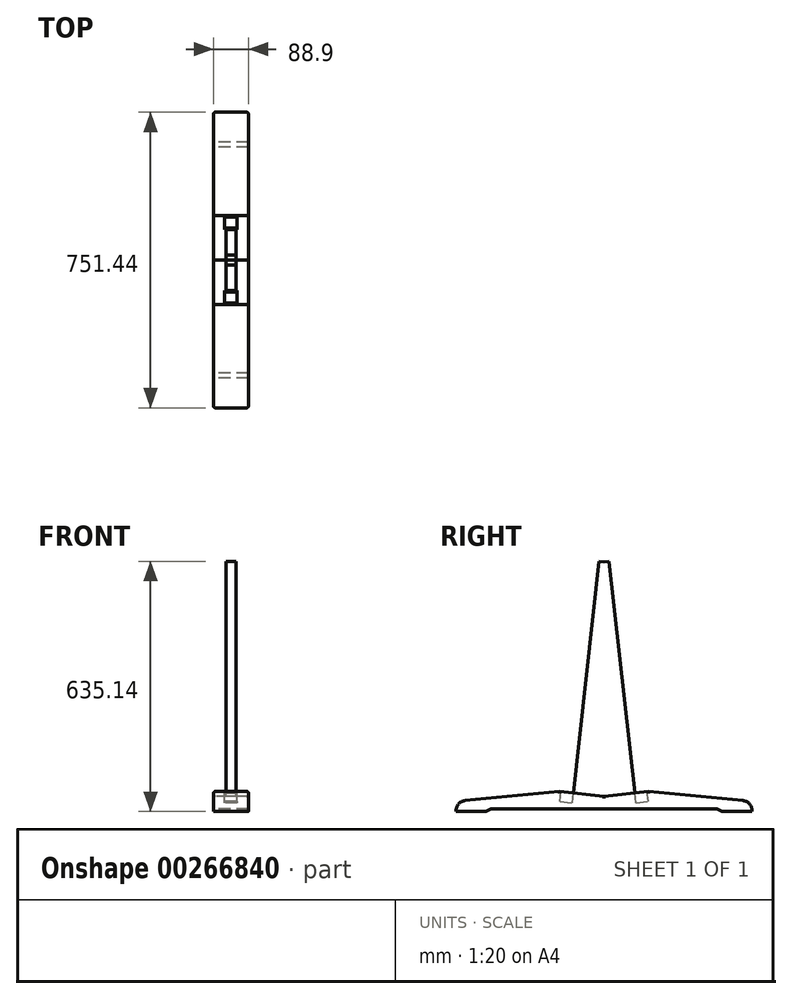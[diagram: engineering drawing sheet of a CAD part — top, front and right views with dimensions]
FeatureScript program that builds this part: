
annotation { "Feature Type Name" : "Feature", "Feature Type Description" : "" }
export const myFeature = defineFeature(function(context is Context, id is Id, definition is map)
    precondition{}
    {
        {
            var Q0;
            Q0=qCreatedBy(makeId("Right.planeOp"),FACE);
            var sketch = newSketch(context, id + "F0", { "sketchPlane" : qUnion([Q0])});
            skLineSegment(sketch, "E0", {"start": v(0, 83.9) * mm, "end": v(-112.69, 96.43) * mm});
            skLineSegment(sketch, "E1", {"start": v(-112.69, 96.43) * mm, "end": v(-352.76, 73.25) * mm});
            skLineSegment(sketch, "E2", {"start": v(-375.72, 47.96) * mm, "end": v(-375.72, 45.63) * mm});
            skLineSegment(sketch, "E3", {"start": v(-375.72, 45.63) * mm, "end": v(-299.52, 45.63) * mm});
            skLineSegment(sketch, "E4", {"start": v(-299.52, 45.63) * mm, "end": v(-286.82, 51.98) * mm});
            skLineSegment(sketch, "E5", {"start": v(-286.82, 51.98) * mm, "end": v(0, 51.98) * mm});
            skLineSegment(sketch, "E6", {"start": v(0, 83.9) * mm, "end": v(0, 51.98) * mm});
            skLineSegment(sketch, "E7.MirrorCS", {"start": v(0, 83.9) * mm, "end": v(112.69, 96.43) * mm});
            skLineSegment(sketch, "E8.MirrorCS", {"start": v(112.69, 96.43) * mm, "end": v(352.76, 73.25) * mm});
            skLineSegment(sketch, "E9.MirrorCS", {"start": v(375.72, 47.96) * mm, "end": v(375.72, 45.63) * mm});
            skLineSegment(sketch, "E10.MirrorCS", {"start": v(375.72, 45.63) * mm, "end": v(299.52, 45.63) * mm});
            skLineSegment(sketch, "E11.MirrorCS", {"start": v(286.82, 51.98) * mm, "end": v(0, 51.98) * mm});
            skLineSegment(sketch, "E12.MirrorCS", {"start": v(299.52, 45.63) * mm, "end": v(286.82, 51.98) * mm});
            skPoint(sketch, "E13.visualSharp", {"position": v(-375.72, 71.03) * mm});
            skArc(sketch, "E13.filletArc", {"start": v(-352.76, 73.25) * mm, "mid": v(-369.12, 65.04) * mm, "end": v(-375.72, 47.96) * mm});
            skPoint(sketch, "E14.visualSharp", {"position": v(375.72, 71.03) * mm});
            skArc(sketch, "E14.filletArc", {"start": v(375.72, 47.96) * mm, "mid": v(369.12, 65.04) * mm, "end": v(352.76, 73.25) * mm});
            skSolve(sketch);
        }
        {
            var Q0;
            Q0 = qSketchRegion(id + "F0", true);
            extrude(context, id + "F1", {"entities" : qUnion([Q0]), "endBound" : BoundingType.SYMMETRIC, "depth" : 88.9 * mm});
        }
        {
            var Q0;
            Q0=makeQuery(id+"F1.opExtrude","SWEPT_FACE",FACE,{"disambiguationData":[OSD([sQuery(id+"F0.wireOp",EDGE,"E0")])]});
            var sketch = newSketch(context, id + "F2", { "sketchPlane" : qUnion([Q0])});
            skLineSegment(sketch, "E15.bottom", {"start": v(15.88, -119.47) * mm, "end": v(-15.88, -119.47) * mm});
            skLineSegment(sketch, "E15.top", {"start": v(15.87, -87.72) * mm, "end": v(-15.88, -87.72) * mm});
            skLineSegment(sketch, "E15.left", {"start": v(15.88, -119.47) * mm, "end": v(15.87, -87.72) * mm});
            skLineSegment(sketch, "E15.right", {"start": v(-15.88, -119.47) * mm, "end": v(-15.88, -87.72) * mm});
            skSolve(sketch);
        }
        {
            var Q0;
            Q0=makeQuery(id+"F2.imprint","IMPRINT",FACE,{"disambiguationData":[TD([[makeQuery(id+"F2.imprint","IMPRINT",EDGE,{"derivedFrom":sQuery(id+"F2.wireOp",EDGE,"E15.bottom")}),-1.0]])]});
            extrude(context, id + "F3", {"entities" : qUnion([Q0]), "operationType" : NewBodyOperationType.REMOVE, "oppositeDirection" : true, "depth" : 25.4 * mm});
        }
        {
            var Q0;
            Q0=makeQuery(id+"F1.opExtrude","SWEPT_FACE",FACE,{"disambiguationData":[OSD([sQuery(id+"F0.wireOp",EDGE,"E7.MirrorCS")])]});
            var sketch = newSketch(context, id + "F4", { "sketchPlane" : qUnion([Q0])});
            skLineSegment(sketch, "E16.bottom", {"start": v(-15.87, 87.72) * mm, "end": v(15.88, 87.72) * mm});
            skLineSegment(sketch, "E16.top", {"start": v(-15.88, 119.47) * mm, "end": v(15.88, 119.47) * mm});
            skLineSegment(sketch, "E16.left", {"start": v(-15.88, 87.72) * mm, "end": v(-15.88, 119.47) * mm});
            skLineSegment(sketch, "E16.right", {"start": v(15.88, 87.72) * mm, "end": v(15.87, 119.47) * mm});
            skPoint(sketch, "E16.middle", {"position": v(0, 103.6) * mm});
            skSolve(sketch);
        }
        {
            var Q0;
            Q0=makeQuery(id+"F4.imprint","IMPRINT",FACE,{"disambiguationData":[TD([[makeQuery(id+"F4.imprint","IMPRINT",EDGE,{"derivedFrom":sQuery(id+"F4.wireOp",EDGE,"E16.bottom")}),1.0]])]});
            extrude(context, id + "F5", {"entities" : qUnion([Q0]), "operationType" : NewBodyOperationType.REMOVE, "oppositeDirection" : true, "depth" : 25.4 * mm});
        }
        {
            var Q0;
            Q0=makeQuery(id+"F1.opExtrude","CAP_EDGE",EDGE,{"disambiguationData":[OSD([sQuery(id+"F0.wireOp",EDGE,"E8.MirrorCS")])],"isStart":true});
            var Q1;
            Q1=makeQuery(id+"F1.opExtrude","CAP_EDGE",EDGE,{"disambiguationData":[OSD([sQuery(id+"F0.wireOp",EDGE,"E1")])],"isStart":true});
            var Q2;
            Q2=makeQuery(id+"F1.opExtrude","CAP_EDGE",EDGE,{"disambiguationData":[OSD([sQuery(id+"F0.wireOp",EDGE,"E0")])],"isStart":true});
            var Q3;
            Q3=makeQuery(id+"F1.opExtrude","CAP_EDGE",EDGE,{"disambiguationData":[OSD([sQuery(id+"F0.wireOp",EDGE,"E7.MirrorCS")])],"isStart":true});
            var Q4;
            Q4=makeQuery(id+"F1.opExtrude","CAP_EDGE",EDGE,{"disambiguationData":[OSD([sQuery(id+"F0.wireOp",EDGE,"E14.filletArc")])],"isStart":false});
            var Q5;
            Q5=makeQuery(id+"F1.opExtrude","CAP_EDGE",EDGE,{"disambiguationData":[OSD([sQuery(id+"F0.wireOp",EDGE,"E8.MirrorCS")])],"isStart":false});
            var Q6;
            Q6=makeQuery(id+"F1.opExtrude","CAP_EDGE",EDGE,{"disambiguationData":[OSD([sQuery(id+"F0.wireOp",EDGE,"E7.MirrorCS")])],"isStart":false});
            var Q7;
            Q7=makeQuery(id+"F1.opExtrude","CAP_EDGE",EDGE,{"disambiguationData":[OSD([sQuery(id+"F0.wireOp",EDGE,"E0")])],"isStart":false});
            var Q8;
            Q8=makeQuery(id+"F1.opExtrude","CAP_EDGE",EDGE,{"disambiguationData":[OSD([sQuery(id+"F0.wireOp",EDGE,"E1")])],"isStart":false});
            var Q9;
            Q9=makeQuery(id+"F1.opExtrude","CAP_EDGE",EDGE,{"disambiguationData":[OSD([sQuery(id+"F0.wireOp",EDGE,"E13.filletArc")])],"isStart":false});
            fillet(context, id + "F6", {"entities" : qUnion([Q0, Q1, Q2, Q3, Q4, Q5, Q6, Q7, Q8, Q9]), "radius" : 5.08 * mm, "tangentPropagation" : true, "allowEdgeOverflow" : false});
        }
        {
            var Q0;
            Q0=qCreatedBy(makeId("Right.planeOp"),FACE);
            var sketch = newSketch(context, id + "F7", { "sketchPlane" : qUnion([Q0])});
            skLineSegment(sketch, "E17", {"start": v(0, 83.9) * mm, "end": v(-77.98, 92.57) * mm});
            skLineSegment(sketch, "E18", {"start": v(-77.98, 92.57) * mm, "end": v(-12.62, 680.77) * mm});
            skLineSegment(sketch, "E19", {"start": v(-12.62, 680.77) * mm, "end": v(0, 679.37) * mm});
            skLineSegment(sketch, "E20", {"start": v(0, 679.37) * mm, "end": v(0, 83.9) * mm});
            skLineSegment(sketch, "E21.MirrorCS", {"start": v(77.98, 92.57) * mm, "end": v(12.62, 680.77) * mm});
            skLineSegment(sketch, "E22.MirrorCS", {"start": v(0, 83.9) * mm, "end": v(77.98, 92.57) * mm});
            skLineSegment(sketch, "E23.MirrorCS", {"start": v(12.62, 680.77) * mm, "end": v(0, 679.37) * mm});
            skSolve(sketch);
        }
        {
            var Q0;
            Q0=makeQuery(id+"F7.imprint","IMPRINT",FACE,{"disambiguationData":[TD([[makeQuery(id+"F7.imprint","IMPRINT",EDGE,{"derivedFrom":sQuery(id+"F7.wireOp",EDGE,"E17")}),-1.0]])]});
            var Q1;
            Q1=makeQuery(id+"F7.imprint","IMPRINT",FACE,{"disambiguationData":[TD([[makeQuery(id+"F7.imprint","IMPRINT",EDGE,{"derivedFrom":sQuery(id+"F7.wireOp",EDGE,"E20")}),1.0]])]});
            extrude(context, id + "F8", {"entities" : qUnion([Q0, Q1]), "endBound" : BoundingType.SYMMETRIC, "depth" : 25.4 * mm});
        }
    });
